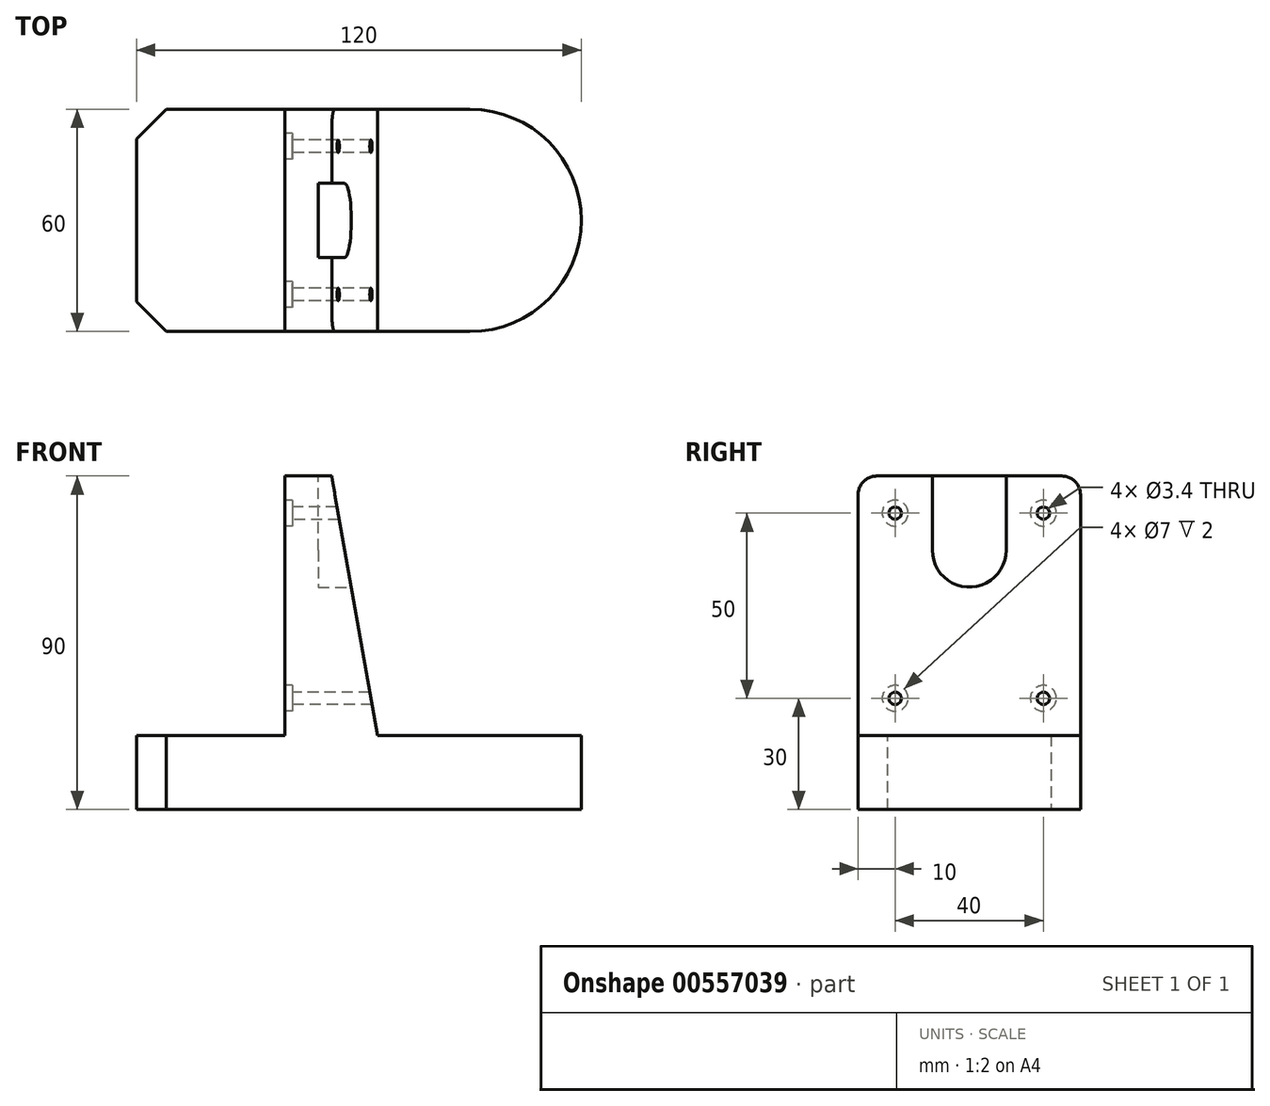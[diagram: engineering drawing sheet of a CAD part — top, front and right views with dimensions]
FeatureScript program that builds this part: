
annotation { "Feature Type Name" : "Feature", "Feature Type Description" : "" }
export const myFeature = defineFeature(function(context is Context, id is Id, definition is map)
    precondition{}
    {
        {
            var Q0;
            Q0=qCreatedBy(makeId("Front.planeOp"),FACE);
            var sketch = newSketch(context, id + "F0", { "sketchPlane" : qUnion([Q0])});
            skLineSegment(sketch, "E0", {"start": v(0, 0) * mm, "end": v(120, 0) * mm});
            skLineSegment(sketch, "E1", {"start": v(0, 0) * mm, "end": v(0, 20) * mm});
            skLineSegment(sketch, "E2", {"start": v(0, 20) * mm, "end": v(40, 20) * mm});
            skLineSegment(sketch, "E3", {"start": v(120, 0) * mm, "end": v(120, 20) * mm});
            skLineSegment(sketch, "E4", {"start": v(65, 20) * mm, "end": v(120, 20) * mm});
            skLineSegment(sketch, "E5", {"start": v(65, 20) * mm, "end": v(65, 90) * mm});
            skLineSegment(sketch, "E6", {"start": v(40, 20) * mm, "end": v(40, 90) * mm});
            skLineSegment(sketch, "E7", {"start": v(40, 90) * mm, "end": v(65, 90) * mm});
            skSolve(sketch);
        }
        {
            var Q0;
            Q0 = qSketchRegion(id + "F0", true);
            extrude(context, id + "F1", {"entities" : qUnion([Q0]), "endBound" : BoundingType.SYMMETRIC, "depth" : 60 * mm, "offsetDistance" : 25 * mm});
        }
        {
            var Q0;
            Q0=makeQuery(id+"F1.opExtrude","CAP_EDGE",EDGE,{"disambiguationData":[OSD([sQuery(id+"F0.wireOp",EDGE,"E3")])],"isStart":false});
            var Q1;
            Q1=makeQuery(id+"F1.opExtrude","CAP_EDGE",EDGE,{"disambiguationData":[OSD([sQuery(id+"F0.wireOp",EDGE,"E3")])],"isStart":true});
            fillet(context, id + "F2", {"entities" : qUnion([Q0, Q1]), "radius" : 30 * mm, "tangentPropagation" : true, "allowEdgeOverflow" : false});
        }
        {
            var Q0;
            Q0=makeQuery(id+"F1.opExtrude","SWEPT_FACE",FACE,{"disambiguationData":[OSD([sQuery(id+"F0.wireOp",EDGE,"E6")])]});
            var sketch = newSketch(context, id + "F3", { "sketchPlane" : qUnion([Q0])});
            skLineSegment(sketch, "E8", {"start": v(-20, 30) * mm, "end": v(20, 30) * mm, "construction": true});
            skLineSegment(sketch, "E9", {"start": v(0, 0) * mm, "end": v(0, 92.48) * mm, "construction": true});
            skPoint(sketch, "E9.endSnap0", {"position": v(0, 90) * mm});
            skLineSegment(sketch, "E10", {"start": v(-20, 30) * mm, "end": v(-20, 80) * mm, "construction": true});
            skLineSegment(sketch, "E11", {"start": v(-20, 80) * mm, "end": v(20, 80) * mm, "construction": true});
            skLineSegment(sketch, "E12", {"start": v(20, 80) * mm, "end": v(20, 30) * mm, "construction": true});
            skCircle(sketch, "E13", {"center": v(-20, 80) * mm, "radius": 3.5 * mm});
            skSolve(sketch);
        }
        {
            var Q0;
            Q0=sQuery(id+"F3.wireOp",VERTEX,"E13.center");
            var Q1;
            Q1=sQuery(id+"F3.wireOp",VERTEX,"E8.start");
            var Q2;
            Q2=sQuery(id+"F3.wireOp",VERTEX,"E12.end");
            var Q3;
            Q3=sQuery(id+"F3.wireOp",VERTEX,"E12.start");
            var Q4;
            Q4=makeQuery(id+"F1.opExtrude","SWEPT_BODY",BODY,{"disambiguationData":[OSD([sQuery(id+"F0.wireOp",EDGE,"E0"),sQuery(id+"F0.wireOp",EDGE,"E1"),sQuery(id+"F0.wireOp",EDGE,"E2"),sQuery(id+"F0.wireOp",EDGE,"E3"),sQuery(id+"F0.wireOp",EDGE,"E4"),sQuery(id+"F0.wireOp",EDGE,"E5"),sQuery(id+"F0.wireOp",EDGE,"E6"),sQuery(id+"F0.wireOp",EDGE,"E7")])]});
            hole(context, id + "F4", {"style" : HoleStyle.C_BORE, "endStyle" : HoleEndStyle.THROUGH, "holeDiameter" : 3.4 * mm, "cBoreDiameter" : 7 * mm, "cBoreDepth" : 2 * mm, "isTappedThrough" : true, "tappedDepth" : 12 * mm, "tapClearance" : 3, "locations" : qUnion([Q0, Q1, Q2, Q3]), "scope" : qUnion([Q4])});
        }
        {
            var Q0;
            Q0=makeQuery(id+"F1.opExtrude","CAP_EDGE",EDGE,{"disambiguationData":[OSD([sQuery(id+"F0.wireOp",EDGE,"E1")])],"isStart":true});
            var Q1;
            Q1=makeQuery(id+"F1.opExtrude","CAP_EDGE",EDGE,{"disambiguationData":[OSD([sQuery(id+"F0.wireOp",EDGE,"E1")])],"isStart":false});
            chamfer(context, id + "F5", {"entities" : qUnion([Q0, Q1]), "width" : 8 * mm, "tangentPropagation" : true});
        }
        {
            var Q0;
            Q0=makeQuery(id+"F1.opExtrude","CAP_FACE",FACE,{"disambiguationData":[OSD([sQuery(id+"F0.wireOp",EDGE,"E0"),sQuery(id+"F0.wireOp",EDGE,"E1"),sQuery(id+"F0.wireOp",EDGE,"E2"),sQuery(id+"F0.wireOp",EDGE,"E3"),sQuery(id+"F0.wireOp",EDGE,"E4"),sQuery(id+"F0.wireOp",EDGE,"E5"),sQuery(id+"F0.wireOp",EDGE,"E6"),sQuery(id+"F0.wireOp",EDGE,"E7")])],"isStart":false});
            var sketch = newSketch(context, id + "F6", { "sketchPlane" : qUnion([Q0])});
            skLineSegment(sketch, "E14", {"start": v(65, 20) * mm, "end": v(52.66, 90) * mm});
            skSolve(sketch);
        }
        {
            var Q0;
            Q0=makeQuery(id+"F1.opExtrude","SWEPT_FACE",FACE,{"disambiguationData":[OSD([sQuery(id+"F0.wireOp",EDGE,"E5")])]});
            var sketch = newSketch(context, id + "F7", { "sketchPlane" : qUnion([Q0])});
            skLineSegment(sketch, "E15", {"start": v(0, -24) * mm, "end": v(0, 77.1) * mm, "construction": true});
            skLineSegment(sketch, "E16", {"start": v(-10, 70) * mm, "end": v(10, 70) * mm, "construction": true});
            skCircle(sketch, "E17", {"center": v(0, 70) * mm, "radius": 10 * mm});
            skLineSegment(sketch, "E18", {"start": v(-10, 70) * mm, "end": v(-10, 90) * mm});
            skLineSegment(sketch, "E19", {"start": v(10, 70) * mm, "end": v(10, 90) * mm});
            skSolve(sketch);
        }
        {
            var Q0;
            Q0=makeQuery(id+"F1.opExtrude","CAP_FACE",FACE,{"disambiguationData":[OSD([sQuery(id+"F0.wireOp",EDGE,"E0"),sQuery(id+"F0.wireOp",EDGE,"E1"),sQuery(id+"F0.wireOp",EDGE,"E2"),sQuery(id+"F0.wireOp",EDGE,"E3"),sQuery(id+"F0.wireOp",EDGE,"E4"),sQuery(id+"F0.wireOp",EDGE,"E5"),sQuery(id+"F0.wireOp",EDGE,"E6"),sQuery(id+"F0.wireOp",EDGE,"E7")])],"isStart":false});
            var sketch = newSketch(context, id + "F8", { "sketchPlane" : qUnion([Q0])});
            skLineSegment(sketch, "E20", {"start": v(65, 60) * mm, "end": v(49, 60) * mm});
            skLineSegment(sketch, "E21", {"start": v(49, 60) * mm, "end": v(49, 90) * mm});
            skSolve(sketch);
        }
        {
            var Q0;
            Q0=makeQuery(id+"F1.opExtrude","SWEPT_FACE",FACE,{"disambiguationData":[OSD([sQuery(id+"F0.wireOp",EDGE,"E6")])]});
            var Q1;
            Q1=sQuery(id+"F8.wireOp",VERTEX,"E21.start");
            cPlane(context, id + "F9", {"entities" : qUnion([Q0, Q1]), "cplaneType" : CPlaneType.PLANE_POINT, "offset" : 25 * mm, "width" : 150 * mm, "height" : 150 * mm});
        }
        {
            var Q0;
            {var subQ0=sQuery(id+"F7.wireOp",EDGE,"E18");Q0=makeQuery(id+"F7.imprint","IMPRINT",FACE,{"disambiguationData":[TD([[makeQuery(id+"F7.imprint","IMPRINT",EDGE,{"derivedFrom":subQ0}),-1.0]])]});}
            var Q1;
            {var subQ0=sQuery(id+"F7.wireOp",EDGE,"E17");var subQ1=makeQuery(id+"F7.imprint","INTERSECT",VERTEX,{"derivedFrom":[subQ0,sQuery(id+"F7.wireOp",EDGE,"E18")]});Q1=makeQuery(id+"F7.imprint","IMPRINT",FACE,{"disambiguationData":[TD([[makeQuery(id+"F7.imprint","IMPRINT",EDGE,{"disambiguationData":[TD([[subQ1,1.0]])],"derivedFrom":subQ0}),1.0]])]});}
            var Q2;
            Q2=qCreatedBy(id+"F9.planeOp",FACE);
            extrude(context, id + "F10", {"entities" : qUnion([Q0, Q1]), "operationType" : NewBodyOperationType.REMOVE, "endBound" : BoundingType.UP_TO_SURFACE, "oppositeDirection" : true, "depth" : 25 * mm, "endBoundEntityFace" : qUnion([Q2]), "offsetDistance" : 25 * mm});
        }
        {
            var Q0;
            {var subQ0=sQuery(id+"F6.wireOp",EDGE,"E14");Q0=makeQuery(id+"F6.imprint","IMPRINT",FACE,{"disambiguationData":[TD([[makeQuery(id+"F6.imprint","IMPRINT",EDGE,{"derivedFrom":subQ0}),-1.0]])]});}
            extrude(context, id + "F11", {"entities" : qUnion([Q0]), "operationType" : NewBodyOperationType.REMOVE, "endBound" : BoundingType.THROUGH_ALL, "oppositeDirection" : true, "depth" : 25 * mm, "offsetDistance" : 25 * mm});
        }
        {
            var Q0;
            Q0=makeQuery(id+"F1.opExtrude","CAP_EDGE",EDGE,{"disambiguationData":[OSD([sQuery(id+"F0.wireOp",EDGE,"E7")])],"isStart":false});
            var Q1;
            Q1=makeQuery(id+"F1.opExtrude","CAP_EDGE",EDGE,{"disambiguationData":[OSD([sQuery(id+"F0.wireOp",EDGE,"E7")])],"isStart":true});
            fillet(context, id + "F12", {"entities" : qUnion([Q0, Q1]), "radius" : 5 * mm, "tangentPropagation" : true, "allowEdgeOverflow" : false});
        }
    });
